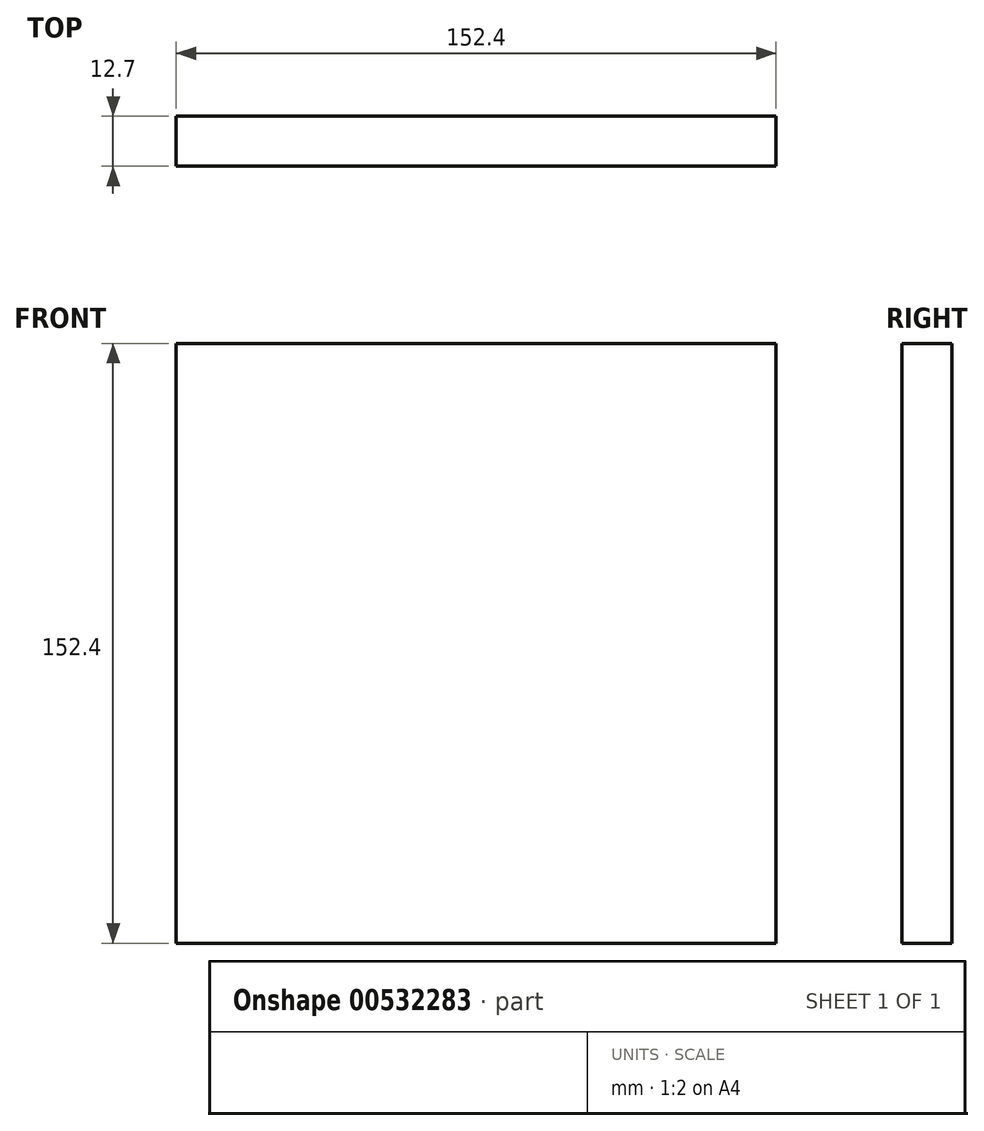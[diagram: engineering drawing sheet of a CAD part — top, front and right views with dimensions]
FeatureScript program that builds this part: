
annotation { "Feature Type Name" : "Feature", "Feature Type Description" : "" }
export const myFeature = defineFeature(function(context is Context, id is Id, definition is map)
    precondition{}
    {
        {
            var Q0;
            Q0=qCreatedBy(makeId("Front.planeOp"),FACE);
            var sketch = newSketch(context, id + "F0", { "sketchPlane" : qUnion([Q0])});
            skLineSegment(sketch, "E0.bottom", {"start": v(0, 0) * mm, "end": v(152.4, 0) * mm});
            skLineSegment(sketch, "E0.top", {"start": v(0, 152.4) * mm, "end": v(152.4, 152.4) * mm});
            skLineSegment(sketch, "E0.left", {"start": v(0, 0) * mm, "end": v(0, 152.4) * mm});
            skLineSegment(sketch, "E0.right", {"start": v(152.4, 0) * mm, "end": v(152.4, 152.4) * mm});
            skSolve(sketch);
        }
        {
            var Q0;
            Q0=makeQuery(id+"F0.imprint","IMPRINT",FACE,{"disambiguationData":[TD([[makeQuery(id+"F0.imprint","IMPRINT",EDGE,{"derivedFrom":sQuery(id+"F0.wireOp",EDGE,"E0.bottom")}),1.0]])]});
            extrude(context, id + "F1", {"entities" : qUnion([Q0]), "depth" : 12.7 * mm, "offsetDistance" : 25.4 * mm});
        }
    });
